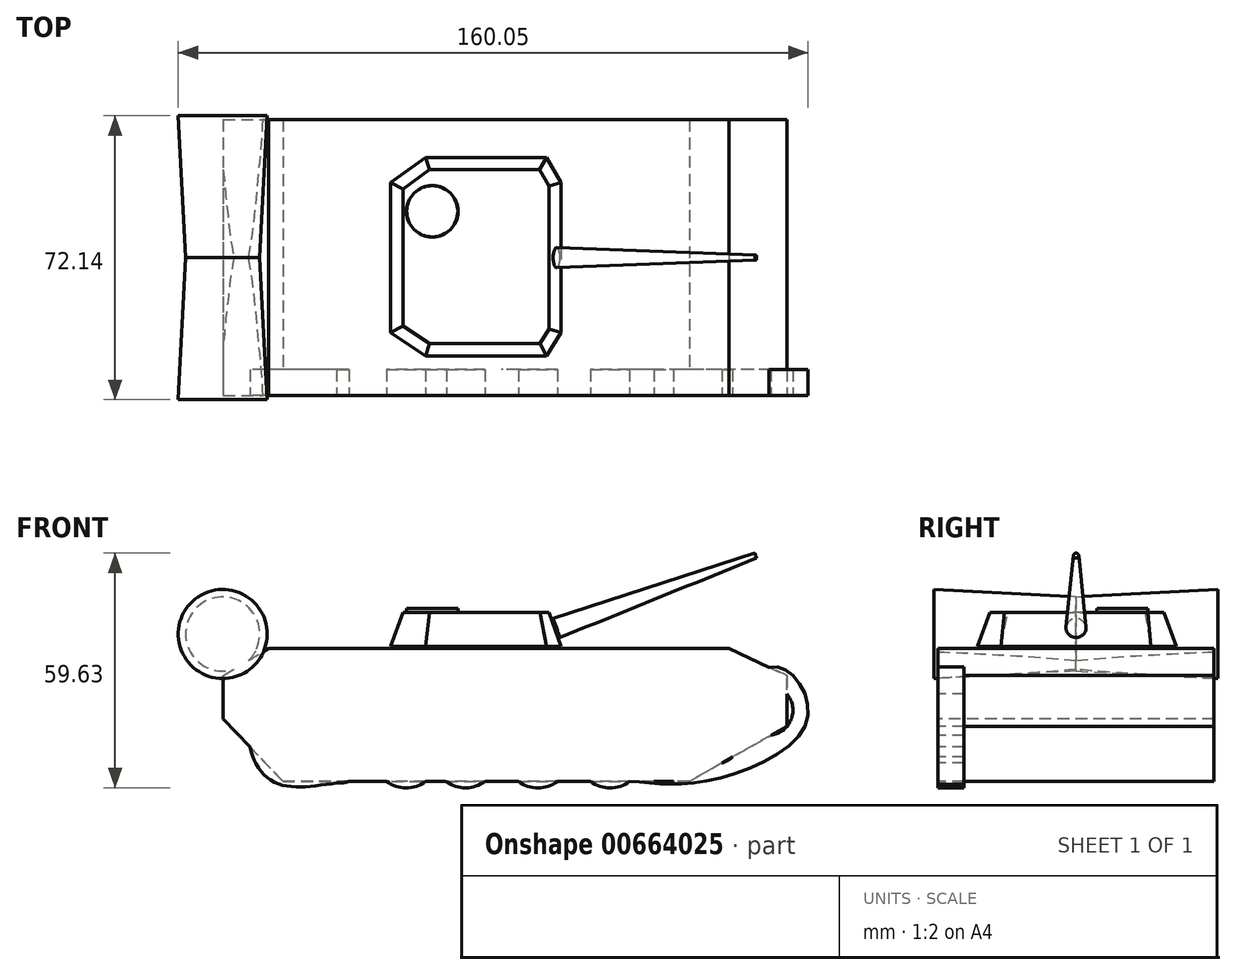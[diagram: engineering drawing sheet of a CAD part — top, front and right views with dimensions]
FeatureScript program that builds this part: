
annotation { "Feature Type Name" : "Feature", "Feature Type Description" : "" }
export const myFeature = defineFeature(function(context is Context, id is Id, definition is map)
    precondition{}
    {
        {
            var Q0;
            Q0=qCreatedBy(makeId("Front.planeOp"),FACE);
            var sketch = newSketch(context, id + "F0", { "sketchPlane" : qUnion([Q0])});
            skLineSegment(sketch, "E0", {"start": v(0, 0) * mm, "end": v(75.97, 0) * mm});
            skLineSegment(sketch, "E1", {"start": v(75.97, 0) * mm, "end": v(100.76, 14) * mm});
            skLineSegment(sketch, "E2", {"start": v(100.76, 14) * mm, "end": v(100.76, 26.85) * mm});
            skLineSegment(sketch, "E3", {"start": v(100.76, 26.85) * mm, "end": v(86.07, 33.74) * mm});
            skLineSegment(sketch, "E4", {"start": v(86.07, 33.74) * mm, "end": v(-30.98, 33.74) * mm});
            skLineSegment(sketch, "E5", {"start": v(-30.98, 33.74) * mm, "end": v(-42.46, 26.85) * mm});
            skLineSegment(sketch, "E6", {"start": v(-42.46, 26.85) * mm, "end": v(-42.46, 15.84) * mm});
            skLineSegment(sketch, "E7", {"start": v(-42.46, 15.84) * mm, "end": v(-27.31, 0) * mm});
            skLineSegment(sketch, "E8", {"start": v(-27.31, 0) * mm, "end": v(0, 0) * mm});
            skSolve(sketch);
        }
        {
            var Q0;
            Q0 = qSketchRegion(id + "F0", true);
            extrude(context, id + "F1", {"entities" : qUnion([Q0]), "endBound" : BoundingType.SYMMETRIC, "oppositeDirection" : true, "depth" : 70.1 * mm, "offsetDistance" : 25.4 * mm});
        }
        {
            var Q0;
            Q0=makeQuery(id+"F1.opExtrude","SWEPT_FACE",FACE,{"disambiguationData":[OSD([sQuery(id+"F0.wireOp",EDGE,"E4")])]});
            cPlane(context, id + "F2", {"entities" : qUnion([Q0]), "cplaneType" : CPlaneType.OFFSET, "offset" : 0.5 * mm, "width" : 152.4 * mm, "height" : 152.4 * mm});
        }
        {
            var Q0;
            Q0=qCreatedBy(id+"F2.planeOp",FACE);
            var sketch = newSketch(context, id + "F3", { "sketchPlane" : qUnion([Q0])});
            skLineSegment(sketch, "E9", {"start": v(0, 0) * mm, "end": v(0, 19.05) * mm});
            skLineSegment(sketch, "E10", {"start": v(0, 19.05) * mm, "end": v(8.95, 25.48) * mm});
            skLineSegment(sketch, "E11", {"start": v(8.95, 25.48) * mm, "end": v(39.7, 25.48) * mm});
            skLineSegment(sketch, "E12", {"start": v(39.7, 25.48) * mm, "end": v(43.38, 19.05) * mm});
            skLineSegment(sketch, "E13", {"start": v(0, 0) * mm, "end": v(0, -19.05) * mm});
            skLineSegment(sketch, "E14", {"start": v(0, -19.05) * mm, "end": v(8.95, -25.02) * mm});
            skLineSegment(sketch, "E15", {"start": v(8.95, -25.02) * mm, "end": v(39.7, -25.02) * mm});
            skLineSegment(sketch, "E16", {"start": v(39.7, -25.02) * mm, "end": v(43.38, -19.05) * mm});
            skLineSegment(sketch, "E17", {"start": v(43.38, -19.05) * mm, "end": v(43.38, 19.05) * mm});
            skSolve(sketch);
        }
        {
            var Q0;
            Q0 = qSketchRegion(id + "F3", true);
            extrude(context, id + "F4", {"entities" : qUnion([Q0]), "depth" : 8.64 * mm, "offsetDistance" : 25.4 * mm, "hasDraft" : true, "draftAngle" : 20 * degree, "draftPullDirection" : true});
        }
        {
            var Q0;
            Q0=makeQuery(id+"F4.opExtrude","SWEPT_FACE",FACE,{"disambiguationData":[OSD([sQuery(id+"F3.wireOp",EDGE,"E17")])]});
            cPlane(context, id + "F5", {"entities" : qUnion([Q0]), "cplaneType" : CPlaneType.OFFSET, "offset" : 0.5 * mm, "width" : 152.4 * mm, "height" : 152.4 * mm});
        }
        {
            var Q0;
            Q0=qCreatedBy(id+"F5.planeOp",FACE);
            var sketch = newSketch(context, id + "F6", { "sketchPlane" : qUnion([Q0])});
            skCircle(sketch, "E18", {"center": v(0, 22.16) * mm, "radius": 2.55 * mm});
            skSolve(sketch);
        }
        {
            var Q0;
            Q0 = qSketchRegion(id + "F6", true);
            extrude(context, id + "F7", {"entities" : qUnion([Q0]), "depth" : 53.85 * mm, "offsetDistance" : 25.4 * mm, "hasDraft" : true, "draftAngle" : 2 * degree, "draftPullDirection" : true});
        }
        {
            var Q0;
            Q0=qCreatedBy(makeId("Front.planeOp"),FACE);
            var sketch = newSketch(context, id + "F8", { "sketchPlane" : qUnion([Q0])});
            skCircle(sketch, "E19", {"center": v(-42.62, 37.44) * mm, "radius": 9.42 * mm});
            skSolve(sketch);
        }
        {
            var Q0;
            Q0 = qSketchRegion(id + "F8", true);
            extrude(context, id + "F9", {"entities" : qUnion([Q0]), "operationType" : NewBodyOperationType.ADD, "endBound" : BoundingType.SYMMETRIC, "oppositeDirection" : true, "depth" : 72.14 * mm, "offsetDistance" : 25.4 * mm, "hasDraft" : true, "draftAngle" : 3 * degree});
        }
        {
            var Q0;
            Q0=makeQuery(id+"F4.opExtrude","CAP_FACE",FACE,{"disambiguationData":[OSD([sQuery(id+"F3.wireOp",EDGE,"E9"),sQuery(id+"F3.wireOp",EDGE,"E10"),sQuery(id+"F3.wireOp",EDGE,"E11"),sQuery(id+"F3.wireOp",EDGE,"E12"),sQuery(id+"F3.wireOp",EDGE,"E13"),sQuery(id+"F3.wireOp",EDGE,"E14"),sQuery(id+"F3.wireOp",EDGE,"E15"),sQuery(id+"F3.wireOp",EDGE,"E16"),sQuery(id+"F3.wireOp",EDGE,"E17")])],"isStart":false});
            cPlane(context, id + "F10", {"entities" : qUnion([Q0]), "cplaneType" : CPlaneType.OFFSET, "offset" : 0 * mm, "width" : 152.4 * mm, "height" : 152.4 * mm});
        }
        {
            var Q0;
            Q0=qCreatedBy(id+"F10.planeOp",FACE);
            var sketch = newSketch(context, id + "F11", { "sketchPlane" : qUnion([Q0])});
            skCircle(sketch, "E20", {"center": v(10.62, 11.77) * mm, "radius": 6.54 * mm});
            skSolve(sketch);
        }
        {
            var Q0;
            Q0 = qSketchRegion(id + "F11", true);
            extrude(context, id + "F12", {"entities" : qUnion([Q0]), "operationType" : NewBodyOperationType.ADD, "depth" : 1.02 * mm, "offsetDistance" : 25.4 * mm, "hasDraft" : true, "draftAngle" : 3 * degree, "draftPullDirection" : true});
        }
        {
            var Q0;
            Q0=makeQuery(id+"F1.opExtrude","CAP_FACE",FACE,{"disambiguationData":[OSD([sQuery(id+"F0.wireOp",EDGE,"E0"),sQuery(id+"F0.wireOp",EDGE,"E1"),sQuery(id+"F0.wireOp",EDGE,"E2"),sQuery(id+"F0.wireOp",EDGE,"E3"),sQuery(id+"F0.wireOp",EDGE,"E4"),sQuery(id+"F0.wireOp",EDGE,"E5"),sQuery(id+"F0.wireOp",EDGE,"E6"),sQuery(id+"F0.wireOp",EDGE,"E7"),sQuery(id+"F0.wireOp",EDGE,"E8")])],"isStart":true});
            cPlane(context, id + "F13", {"entities" : qUnion([Q0]), "cplaneType" : CPlaneType.OFFSET, "offset" : 0 * mm, "width" : 152.4 * mm, "height" : 152.4 * mm});
        }
        {
            var Q0;
            Q0=qCreatedBy(id+"F13.planeOp",FACE);
            var sketch = newSketch(context, id + "F14", { "sketchPlane" : qUnion([Q0])});
            skCircle(sketch, "E21", {"center": v(-25.67, 10.51) * mm, "radius": 7.45 * mm});
            skCircle(sketch, "E22", {"center": v(-12.95, 6.74) * mm, "radius": 7.17 * mm});
            skCircle(sketch, "E23", {"center": v(4, 6.74) * mm, "radius": 8.39 * mm});
            skCircle(sketch, "E24", {"center": v(19.07, 6.74) * mm, "radius": 8.38 * mm});
            skCircle(sketch, "E25", {"center": v(37.44, 6.74) * mm, "radius": 8.38 * mm});
            skCircle(sketch, "E26", {"center": v(55.81, 6.74) * mm, "radius": 8.38 * mm});
            skCircle(sketch, "E27", {"center": v(69.47, 6.74) * mm, "radius": 7.18 * mm});
            skCircle(sketch, "E28", {"center": v(82.18, 11.45) * mm, "radius": 7.08 * mm});
            skCircle(sketch, "E29", {"center": v(95.84, 18.05) * mm, "radius": 6.4 * mm});
            skFitSpline(sketch, "E30", {"points": [v(-35.56, 13.34) * mm, v(-26.6, 21.81) * mm, v(-15.3, 17.58) * mm, v(0, 18.99) * mm, v(15.78, 18.05) * mm, v(28.96, 17.1) * mm, v(46.4, 17.1) * mm, v(63.82, 17.1) * mm, v(85.48, 23.23) * mm, v(99.14, 28.88) * mm, v(105.73, 15.22) * mm, v(79.83, 0) * mm, v(60.79, 0) * mm, v(42.42, 0) * mm, v(24.05, 0) * mm, v(8.99, 0) * mm, v(-10.5, 0) * mm, v(-29.9, 0) * mm, v(-35.56, 13.34) * mm]});
            skSolve(sketch);
        }
        {
            var Q0;
            Q0 = qSketchRegion(id + "F14", true);
            extrude(context, id + "F15", {"entities" : qUnion([Q0]), "operationType" : NewBodyOperationType.ADD, "oppositeDirection" : true, "depth" : 6.6 * mm, "offsetDistance" : 25.4 * mm});
        }
    });
